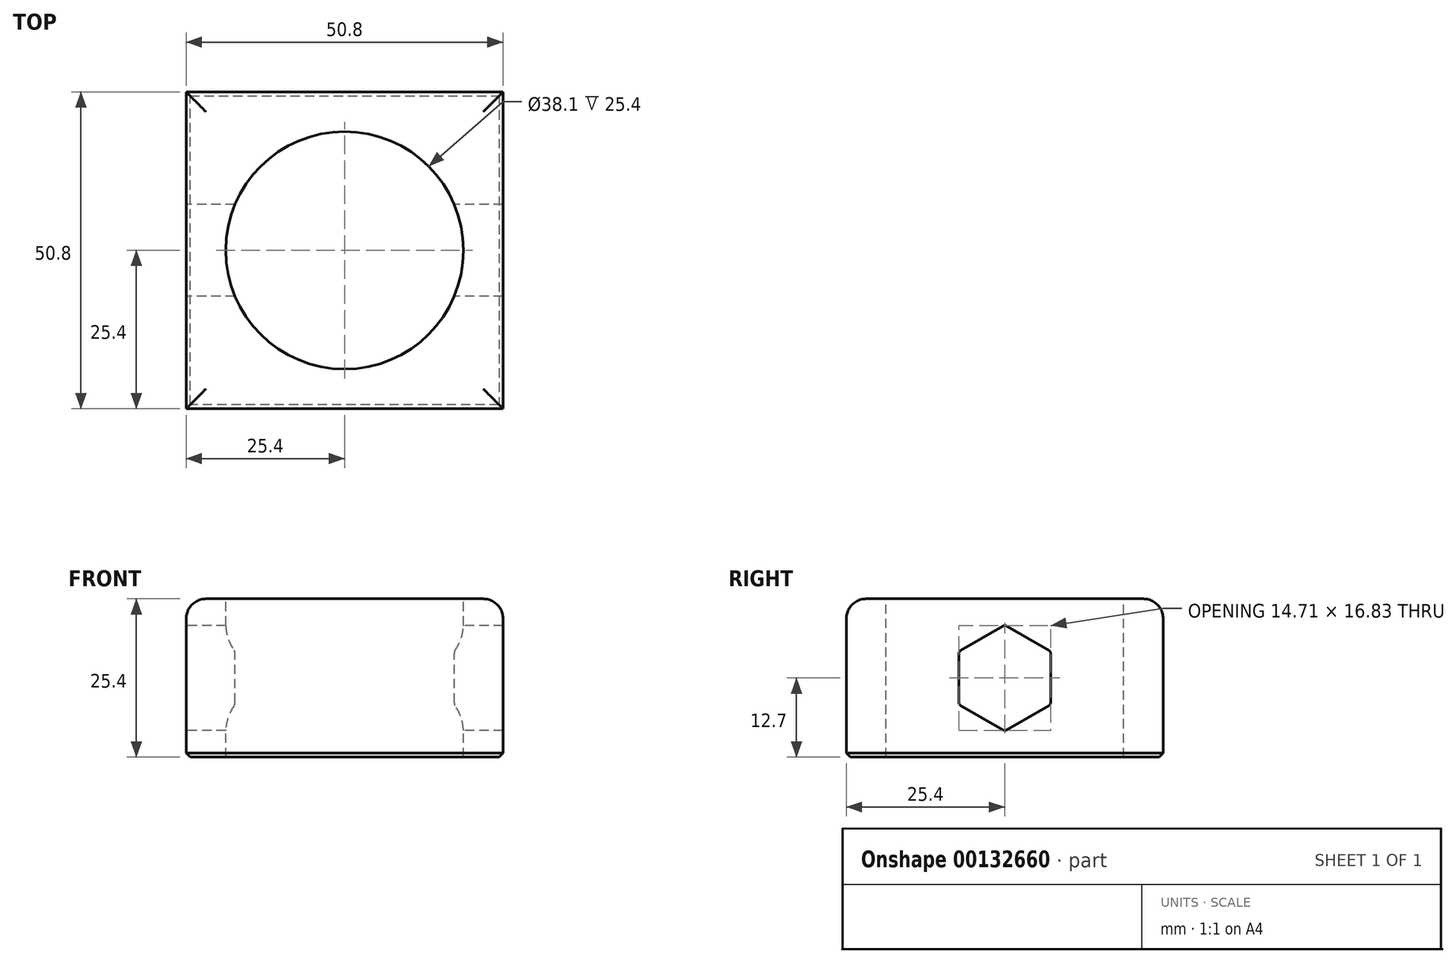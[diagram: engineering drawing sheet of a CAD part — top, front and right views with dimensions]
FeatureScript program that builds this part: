
annotation { "Feature Type Name" : "Feature", "Feature Type Description" : "" }
export const myFeature = defineFeature(function(context is Context, id is Id, definition is map)
    precondition{}
    {
        {
            var Q0;
            Q0=qCreatedBy(makeId("Top.planeOp"),FACE);
            var sketch = newSketch(context, id + "F0", { "sketchPlane" : qUnion([Q0])});
            skLineSegment(sketch, "E0.bottom", {"start": v(25.4, -25.4) * mm, "end": v(-25.4, -25.4) * mm});
            skLineSegment(sketch, "E0.top", {"start": v(25.4, 25.4) * mm, "end": v(-25.4, 25.4) * mm});
            skLineSegment(sketch, "E0.left", {"start": v(25.4, -25.4) * mm, "end": v(25.4, 25.4) * mm});
            skLineSegment(sketch, "E0.right", {"start": v(-25.4, -25.4) * mm, "end": v(-25.4, 25.4) * mm});
            skPoint(sketch, "E0.middle", {"position": v(0, 0) * mm});
            skSolve(sketch);
        }
        {
            var Q0;
            Q0=makeQuery(id+"F0.imprint","IMPRINT",FACE,{"disambiguationData":[TD([[makeQuery(id+"F0.imprint","IMPRINT",EDGE,{"derivedFrom":sQuery(id+"F0.wireOp",EDGE,"E0.bottom")}),-1.0]])]});
            extrude(context, id + "F1", {"entities" : qUnion([Q0]), "oppositeDirection" : true, "depth" : 25.4 * mm});
        }
        {
            var Q0;
            Q0=makeQuery(id+"F1.opExtrude","CAP_FACE",FACE,{"disambiguationData":[OSD([sQuery(id+"F0.wireOp",EDGE,"E0.bottom"),sQuery(id+"F0.wireOp",EDGE,"E0.top"),sQuery(id+"F0.wireOp",EDGE,"E0.left"),sQuery(id+"F0.wireOp",EDGE,"E0.right")])],"isStart":true});
            var sketch = newSketch(context, id + "F2", { "sketchPlane" : qUnion([Q0])});
            skPoint(sketch, "E1", {"position": v(0, 0) * mm});
            skSolve(sketch);
        }
        {
            var Q0;
            Q0=sQuery(id+"F2.wireOp",VERTEX,"E1");
            var Q1;
            Q1=makeQuery(id+"F1.opExtrude","SWEPT_BODY",BODY,{"disambiguationData":[OSD([sQuery(id+"F0.wireOp",EDGE,"E0.bottom"),sQuery(id+"F0.wireOp",EDGE,"E0.top"),sQuery(id+"F0.wireOp",EDGE,"E0.left"),sQuery(id+"F0.wireOp",EDGE,"E0.right")])]});
            hole(context, id + "F3", {"style" : HoleStyle.SIMPLE, "endStyle" : HoleEndStyle.THROUGH, "holeDiameter" : 38.1 * mm, "locations" : qUnion([Q0]), "scope" : qUnion([Q1]), "isTappedThrough" : true});
        }
        {
            var Q0;
            Q0=makeQuery(id+"F1.opExtrude","CAP_EDGE",EDGE,{"disambiguationData":[OSD([sQuery(id+"F0.wireOp",EDGE,"E0.top")])],"isStart":true});
            var Q1;
            Q1=makeQuery(id+"F1.opExtrude","CAP_EDGE",EDGE,{"disambiguationData":[OSD([sQuery(id+"F0.wireOp",EDGE,"E0.left")])],"isStart":true});
            var Q2;
            Q2=makeQuery(id+"F1.opExtrude","CAP_EDGE",EDGE,{"disambiguationData":[OSD([sQuery(id+"F0.wireOp",EDGE,"E0.bottom")])],"isStart":true});
            var Q3;
            Q3=makeQuery(id+"F1.opExtrude","CAP_EDGE",EDGE,{"disambiguationData":[OSD([sQuery(id+"F0.wireOp",EDGE,"E0.right")])],"isStart":true});
            fillet(context, id + "F4", {"entities" : qUnion([Q0, Q1, Q2, Q3]), "radius" : 3.17 * mm, "tangentPropagation" : true, "allowEdgeOverflow" : false});
        }
        {
            var Q0;
            Q0=makeQuery(id+"F1.opExtrude","CAP_EDGE",EDGE,{"disambiguationData":[OSD([sQuery(id+"F0.wireOp",EDGE,"E0.top")])],"isStart":false});
            var Q1;
            Q1=makeQuery(id+"F1.opExtrude","CAP_EDGE",EDGE,{"disambiguationData":[OSD([sQuery(id+"F0.wireOp",EDGE,"E0.right")])],"isStart":false});
            var Q2;
            Q2=makeQuery(id+"F1.opExtrude","CAP_EDGE",EDGE,{"disambiguationData":[OSD([sQuery(id+"F0.wireOp",EDGE,"E0.bottom")])],"isStart":false});
            var Q3;
            Q3=makeQuery(id+"F1.opExtrude","CAP_EDGE",EDGE,{"disambiguationData":[OSD([sQuery(id+"F0.wireOp",EDGE,"E0.left")])],"isStart":false});
            chamfer(context, id + "F5", {"entities" : qUnion([Q0, Q1, Q2, Q3]), "width" : 0.64 * mm, "tangentPropagation" : true});
        }
        {
            var Q0;
            Q0=makeQuery(id+"F1.opExtrude","SWEPT_FACE",FACE,{"disambiguationData":[OSD([sQuery(id+"F0.wireOp",EDGE,"E0.right")])]});
            var sketch = newSketch(context, id + "F6", { "sketchPlane" : qUnion([Q0])});
            skCircle(sketch, "E2.cCircle", {"center": v(0, -12.7) * mm, "radius": 7.36 * mm, "construction": true});
            skLineSegment(sketch, "E2.0", {"start": v(7.36, -8.75) * mm, "end": v(7.36, -16.65) * mm});
            skLineSegment(sketch, "E2.1", {"start": v(7.1, -17.1) * mm, "end": v(0.25, -21.05) * mm});
            skLineSegment(sketch, "E2.2", {"start": v(-0.25, -21.05) * mm, "end": v(-7.1, -17.1) * mm});
            skLineSegment(sketch, "E2.3", {"start": v(-7.36, -16.65) * mm, "end": v(-7.36, -8.75) * mm});
            skLineSegment(sketch, "E2.4", {"start": v(-7.1, -8.3) * mm, "end": v(-0.25, -4.35) * mm});
            skLineSegment(sketch, "E2.5", {"start": v(0.25, -4.35) * mm, "end": v(7.1, -8.3) * mm});
            skPoint(sketch, "E2.0.midPoint", {"position": v(7.36, -12.7) * mm});
            skPoint(sketch, "E3.visualSharp", {"position": v(0, -4.2) * mm});
            skArc(sketch, "E3.filletArc", {"start": v(0.25, -4.35) * mm, "mid": v(0, -4.29) * mm, "end": v(-0.25, -4.35) * mm});
            skPoint(sketch, "E4.visualSharp", {"position": v(7.36, -8.45) * mm});
            skArc(sketch, "E4.filletArc", {"start": v(7.36, -8.75) * mm, "mid": v(7.29, -8.5) * mm, "end": v(7.1, -8.3) * mm});
            skPoint(sketch, "E5.visualSharp", {"position": v(7.36, -16.95) * mm});
            skArc(sketch, "E5.filletArc", {"start": v(7.1, -17.1) * mm, "mid": v(7.29, -16.9) * mm, "end": v(7.36, -16.65) * mm});
            skPoint(sketch, "E6.visualSharp", {"position": v(0, -21.2) * mm});
            skArc(sketch, "E6.filletArc", {"start": v(-0.25, -21.05) * mm, "mid": v(0, -21.11) * mm, "end": v(0.25, -21.05) * mm});
            skPoint(sketch, "E7.visualSharp", {"position": v(-7.36, -16.95) * mm});
            skArc(sketch, "E7.filletArc", {"start": v(-7.36, -16.65) * mm, "mid": v(-7.29, -16.9) * mm, "end": v(-7.1, -17.1) * mm});
            skPoint(sketch, "E8.visualSharp", {"position": v(-7.36, -8.45) * mm});
            skArc(sketch, "E8.filletArc", {"start": v(-7.1, -8.3) * mm, "mid": v(-7.29, -8.5) * mm, "end": v(-7.36, -8.75) * mm});
            skSolve(sketch);
        }
        {
            var Q0;
            Q0=makeQuery(id+"F6.imprint","IMPRINT",FACE,{"disambiguationData":[TD([[makeQuery(id+"F6.imprint","IMPRINT",EDGE,{"derivedFrom":sQuery(id+"F6.wireOp",EDGE,"E2.0")}),-1.0]])]});
            extrude(context, id + "F7", {"entities" : qUnion([Q0]), "operationType" : NewBodyOperationType.REMOVE, "endBound" : BoundingType.THROUGH_ALL, "oppositeDirection" : true, "depth" : 25.4 * mm});
        }
    });
